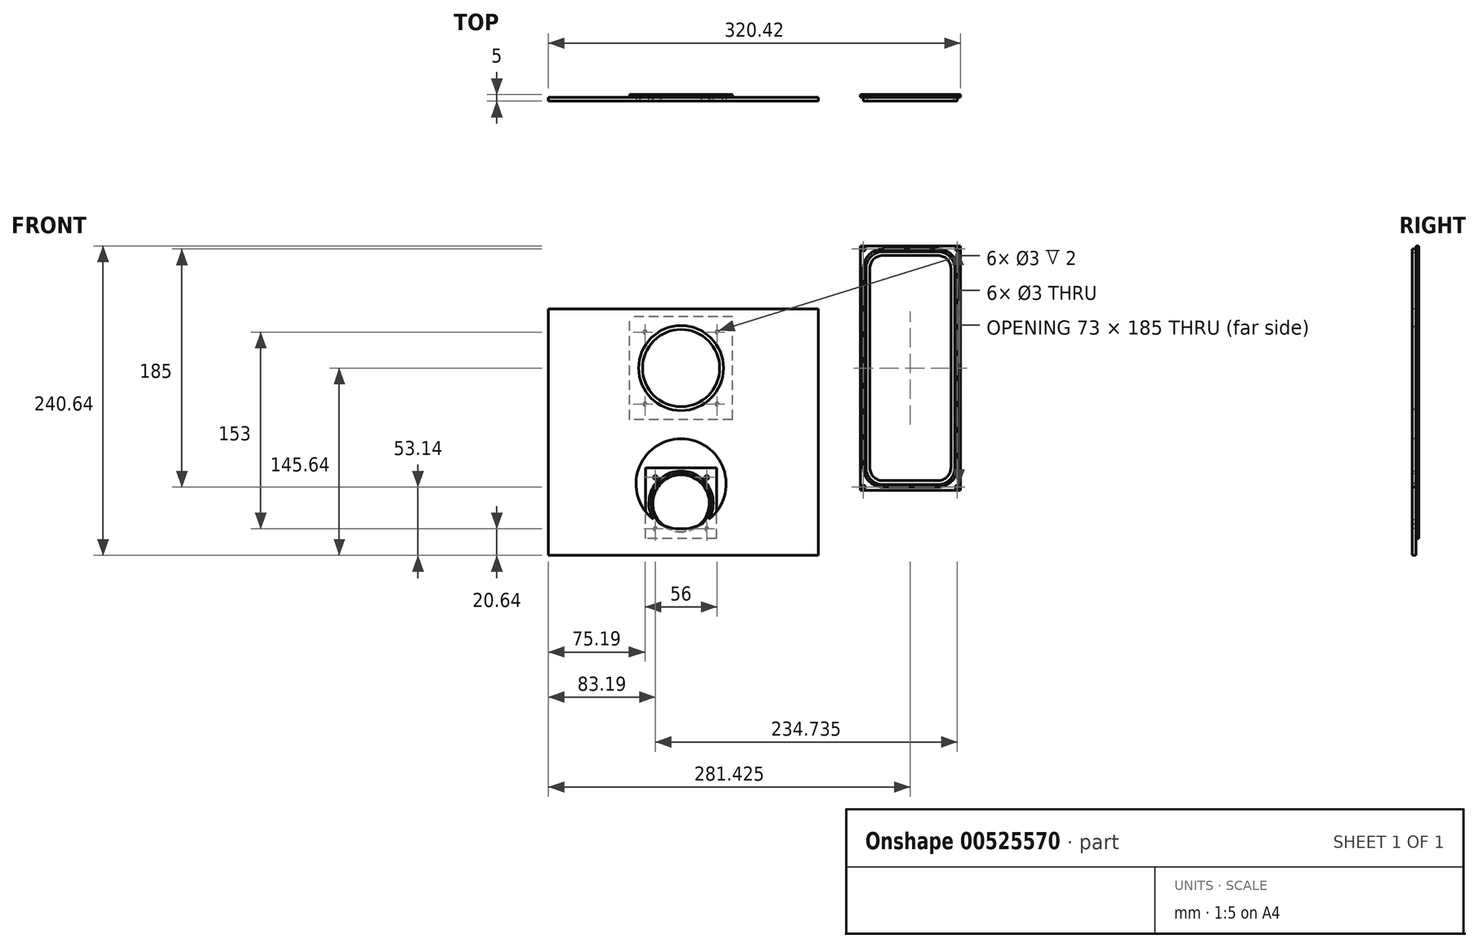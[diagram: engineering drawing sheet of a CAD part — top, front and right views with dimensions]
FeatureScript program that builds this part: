
annotation { "Feature Type Name" : "Feature", "Feature Type Description" : "" }
export const myFeature = defineFeature(function(context is Context, id is Id, definition is map)
    precondition{}
    {
        {
            var Q0;
            Q0=qCreatedBy(makeId("Front.planeOp"),FACE);
            cPlane(context, id + "F0", {"entities" : qUnion([Q0]), "cplaneType" : CPlaneType.OFFSET, "offset" : 5 * mm, "width" : 150 * mm, "height" : 150 * mm});
        }
        {
            var Q0;
            Q0=qCreatedBy(id+"F0.planeOp",FACE);
            var sketch = newSketch(context, id + "F1", { "sketchPlane" : qUnion([Q0])});
            skCircle(sketch, "E0", {"center": v(0, 0) * mm, "radius": 35 * mm});
            skCircle(sketch, "E1", {"center": v(0, -90) * mm, "radius": 35 * mm});
            skLineSegment(sketch, "E2.bottom", {"start": v(-103.2, 46.1) * mm, "end": v(106.7, 46.1) * mm});
            skLineSegment(sketch, "E2.top", {"start": v(-103.2, -145.64) * mm, "end": v(106.7, -145.64) * mm});
            skLineSegment(sketch, "E2.left", {"start": v(-103.2, 46.1) * mm, "end": v(-103.2, -145.64) * mm});
            skLineSegment(sketch, "E2.right", {"start": v(106.7, 46.1) * mm, "end": v(106.7, -145.64) * mm});
            skSolve(sketch);
        }
        {
            var Q0;
            Q0=qSketchRegion(id+"F1",true);
            extrude(context, id + "F2", {"entities" : qUnion([Q0]), "oppositeDirection" : true, "depth" : 3 * mm});
        }
        {
            var Q0;
            Q0=qCreatedBy(makeId("Right.planeOp"),FACE);
            var sketch = newSketch(context, id + "F3", { "sketchPlane" : qUnion([Q0])});
            skLineSegment(sketch, "E3", {"start": v(19.32, 0) * mm, "end": v(-16.11, 0) * mm, "construction": true});
            skLineSegment(sketch, "E4", {"start": v(-5, 35) * mm, "end": v(-5, 33) * mm});
            skLineSegment(sketch, "E5", {"start": v(-5, 33) * mm, "end": v(0, 30) * mm});
            skLineSegment(sketch, "E6", {"start": v(0, 30) * mm, "end": v(0, 35) * mm});
            skLineSegment(sketch, "E7", {"start": v(0, 35) * mm, "end": v(-5, 35) * mm});
            skSolve(sketch);
        }
        {
            var Q0;
            Q0=qSketchRegion(id+"F3",true);
            var Q1;
            Q1=sQuery(id+"F3.wireOp",EDGE,"E3");
            revolve(context, id + "F4", {"entities" : qUnion([Q0]), "axis" : qUnion([Q1]), "revolveType" : RevolveType.FULL});
        }
        {
            var Q0;
            Q0=qCreatedBy(makeId("Front.planeOp"),FACE);
            var sketch = newSketch(context, id + "F5", { "sketchPlane" : qUnion([Q0])});
            skCircle(sketch, "E8", {"center": v(0, 0) * mm, "radius": 35 * mm});
            skLineSegment(sketch, "E9.bottom", {"start": v(40, -40) * mm, "end": v(-40, -40) * mm});
            skLineSegment(sketch, "E9.top", {"start": v(40, 40) * mm, "end": v(-40, 40) * mm});
            skLineSegment(sketch, "E9.left", {"start": v(40, -40) * mm, "end": v(40, 40) * mm});
            skLineSegment(sketch, "E9.right", {"start": v(-40, -40) * mm, "end": v(-40, 40) * mm});
            skCircle(sketch, "E10", {"center": v(-28, 28) * mm, "radius": 1.5 * mm});
            skCircle(sketch, "E11", {"center": v(-28, -28) * mm, "radius": 1.5 * mm});
            skCircle(sketch, "E12", {"center": v(28, 28) * mm, "radius": 1.5 * mm});
            skCircle(sketch, "E13", {"center": v(28, -28) * mm, "radius": 1.5 * mm});
            skSolve(sketch);
        }
        {
            var Q0;
            Q0=qSketchRegion(id+"F5",true);
            extrude(context, id + "F6", {"entities" : qUnion([Q0]), "operationType" : NewBodyOperationType.ADD, "depth" : 2 * mm});
        }
        {
            var Q0;
            Q0=qCreatedBy(makeId("Front.planeOp"),FACE);
            var sketch = newSketch(context, id + "F7", { "sketchPlane" : qUnion([Q0])});
            skLineSegment(sketch, "E14.bottom", {"start": v(217.23, -95) * mm, "end": v(139.23, -95) * mm});
            skLineSegment(sketch, "E14.top", {"start": v(217.23, 95) * mm, "end": v(139.23, 95) * mm});
            skLineSegment(sketch, "E14.left", {"start": v(217.23, -95) * mm, "end": v(217.23, 95) * mm});
            skLineSegment(sketch, "E14.right", {"start": v(139.23, -95) * mm, "end": v(139.23, 95) * mm});
            skPoint(sketch, "E14.middle", {"position": v(178.23, 0) * mm});
            skLineSegment(sketch, "E15.bottom", {"start": v(199.73, -92.5) * mm, "end": v(156.73, -92.5) * mm});
            skLineSegment(sketch, "E15.top", {"start": v(199.73, 92.5) * mm, "end": v(156.73, 92.5) * mm});
            skLineSegment(sketch, "E15.left", {"start": v(214.73, -77.5) * mm, "end": v(214.73, 77.5) * mm});
            skLineSegment(sketch, "E15.right", {"start": v(141.73, -77.5) * mm, "end": v(141.73, 77.5) * mm});
            skPoint(sketch, "E16.visualSharp", {"position": v(141.73, 92.5) * mm});
            skArc(sketch, "E16.filletArc", {"start": v(156.73, 92.5) * mm, "mid": v(146.13, 88.1) * mm, "end": v(141.73, 77.5) * mm});
            skPoint(sketch, "E17.visualSharp", {"position": v(214.73, 92.5) * mm});
            skArc(sketch, "E17.filletArc", {"start": v(214.73, 77.5) * mm, "mid": v(210.34, 88.1) * mm, "end": v(199.73, 92.5) * mm});
            skPoint(sketch, "E18.visualSharp", {"position": v(141.73, -92.5) * mm});
            skArc(sketch, "E18.filletArc", {"start": v(141.73, -77.5) * mm, "mid": v(146.13, -88.1) * mm, "end": v(156.73, -92.5) * mm});
            skPoint(sketch, "E19.visualSharp", {"position": v(214.73, -92.5) * mm});
            skArc(sketch, "E19.filletArc", {"start": v(199.73, -92.5) * mm, "mid": v(210.34, -88.1) * mm, "end": v(214.73, -77.5) * mm});
            skCircle(sketch, "E20", {"center": v(141.73, 92.5) * mm, "radius": 1.5 * mm});
            skCircle(sketch, "E21", {"center": v(214.73, 92.5) * mm, "radius": 1.5 * mm});
            skCircle(sketch, "E22", {"center": v(141.73, -92.5) * mm, "radius": 1.5 * mm});
            skCircle(sketch, "E23", {"center": v(214.73, -92.5) * mm, "radius": 1.5 * mm});
            skSolve(sketch);
        }
        {
            var Q0;
            Q0=makeQuery(id+"F7.imprint","IMPRINT",FACE,{"disambiguationData":[TD([[makeQuery(id+"F7.imprint","IMPRINT",EDGE,{"derivedFrom":sQuery(id+"F7.wireOp",EDGE,"E14.bottom")}),-1.0]])]});
            extrude(context, id + "F8", {"entities" : qUnion([Q0]), "depth" : 2 * mm});
        }
        {
            var Q0;
            Q0=qCreatedBy(makeId("Top.planeOp"),FACE);
            cPlane(context, id + "F9", {"entities" : qUnion([Q0]), "cplaneType" : CPlaneType.OFFSET, "offset" : 77.5 * mm, "oppositeDirection" : true, "width" : 150 * mm, "height" : 150 * mm});
        }
        {
            var Q0;
            Q0=qCreatedBy(id+"F9.planeOp",FACE);
            var sketch = newSketch(context, id + "F10", { "sketchPlane" : qUnion([Q0])});
            skLineSegment(sketch, "E24", {"start": v(141.74, -5) * mm, "end": v(141.74, 0) * mm});
            skLineSegment(sketch, "E25", {"start": v(141.74, 0) * mm, "end": v(146.74, 0) * mm});
            skLineSegment(sketch, "E26", {"start": v(146.74, 0) * mm, "end": v(143.74, -5) * mm});
            skLineSegment(sketch, "E27", {"start": v(143.74, -5) * mm, "end": v(141.74, -5) * mm});
            skSolve(sketch);
        }
        {
            var Q0;
            Q0=qSketchRegion(id+"F10",true);
            var Q1;
            Q1=sQuery(id+"F7.wireOp",EDGE,"E15.right");
            var Q2;
            Q2=sQuery(id+"F7.wireOp",EDGE,"E16.filletArc");
            var Q3;
            Q3=sQuery(id+"F7.wireOp",EDGE,"E15.top");
            var Q4;
            Q4=sQuery(id+"F7.wireOp",EDGE,"E17.filletArc");
            var Q5;
            Q5=sQuery(id+"F7.wireOp",EDGE,"E15.left");
            var Q6;
            Q6=sQuery(id+"F7.wireOp",EDGE,"E19.filletArc");
            var Q7;
            Q7=sQuery(id+"F7.wireOp",EDGE,"E15.bottom");
            var Q8;
            Q8=sQuery(id+"F7.wireOp",EDGE,"E18.filletArc");
            sweep(context, id + "F11", {"operationType" : NewBodyOperationType.ADD, "profiles" : qUnion([Q0]), "path" : qUnion([Q1, Q2, Q3, Q4, Q5, Q6, Q7, Q8])});
        }
        {
            var Q0;
            Q0=qCreatedBy(makeId("Right.planeOp"),FACE);
            var sketch = newSketch(context, id + "F12", { "sketchPlane" : qUnion([Q0])});
            skLineSegment(sketch, "E28", {"start": v(19.32, -105) * mm, "end": v(-16.11, -105) * mm, "construction": true});
            skLineSegment(sketch, "E29", {"start": v(-5, -80) * mm, "end": v(-5, -82) * mm});
            skLineSegment(sketch, "E30", {"start": v(-5, -82) * mm, "end": v(0, -83) * mm});
            skLineSegment(sketch, "E31", {"start": v(0, -83) * mm, "end": v(0, -80) * mm});
            skLineSegment(sketch, "E32", {"start": v(0, -80) * mm, "end": v(-5, -80) * mm});
            skSolve(sketch);
        }
        {
            var Q0;
            Q0=makeQuery(id+"F12.imprint","IMPRINT",FACE,{"disambiguationData":[TD([[makeQuery(id+"F12.imprint","IMPRINT",EDGE,{"derivedFrom":sQuery(id+"F12.wireOp",EDGE,"E29")}),1.0]])]});
            var Q1;
            Q1=sQuery(id+"F12.wireOp",EDGE,"E28");
            revolve(context, id + "F13", {"entities" : qUnion([Q0]), "axis" : qUnion([Q1]), "revolveType" : RevolveType.FULL});
        }
        {
            var Q0;
            Q0=qCreatedBy(makeId("Front.planeOp"),FACE);
            var sketch = newSketch(context, id + "F14", { "sketchPlane" : qUnion([Q0])});
            skCircle(sketch, "E33", {"center": v(0, -105) * mm, "radius": 25 * mm});
            skLineSegment(sketch, "E34.bottom", {"start": v(27.5, -132.5) * mm, "end": v(-27.5, -132.5) * mm});
            skLineSegment(sketch, "E34.top", {"start": v(27.5, -77.5) * mm, "end": v(-27.5, -77.5) * mm});
            skLineSegment(sketch, "E34.left", {"start": v(27.5, -132.5) * mm, "end": v(27.5, -77.5) * mm});
            skLineSegment(sketch, "E34.right", {"start": v(-27.5, -132.5) * mm, "end": v(-27.5, -77.5) * mm});
            skCircle(sketch, "E35", {"center": v(-20, -85) * mm, "radius": 1.5 * mm});
            skCircle(sketch, "E36", {"center": v(-20, -125) * mm, "radius": 1.5 * mm});
            skCircle(sketch, "E37", {"center": v(20, -85) * mm, "radius": 1.5 * mm});
            skCircle(sketch, "E38", {"center": v(20, -125) * mm, "radius": 1.5 * mm});
            skSolve(sketch);
        }
        {
            var Q0;
            Q0=qSketchRegion(id+"F14",true);
            extrude(context, id + "F15", {"entities" : qUnion([Q0]), "operationType" : NewBodyOperationType.ADD, "depth" : 2 * mm});
        }
    });
